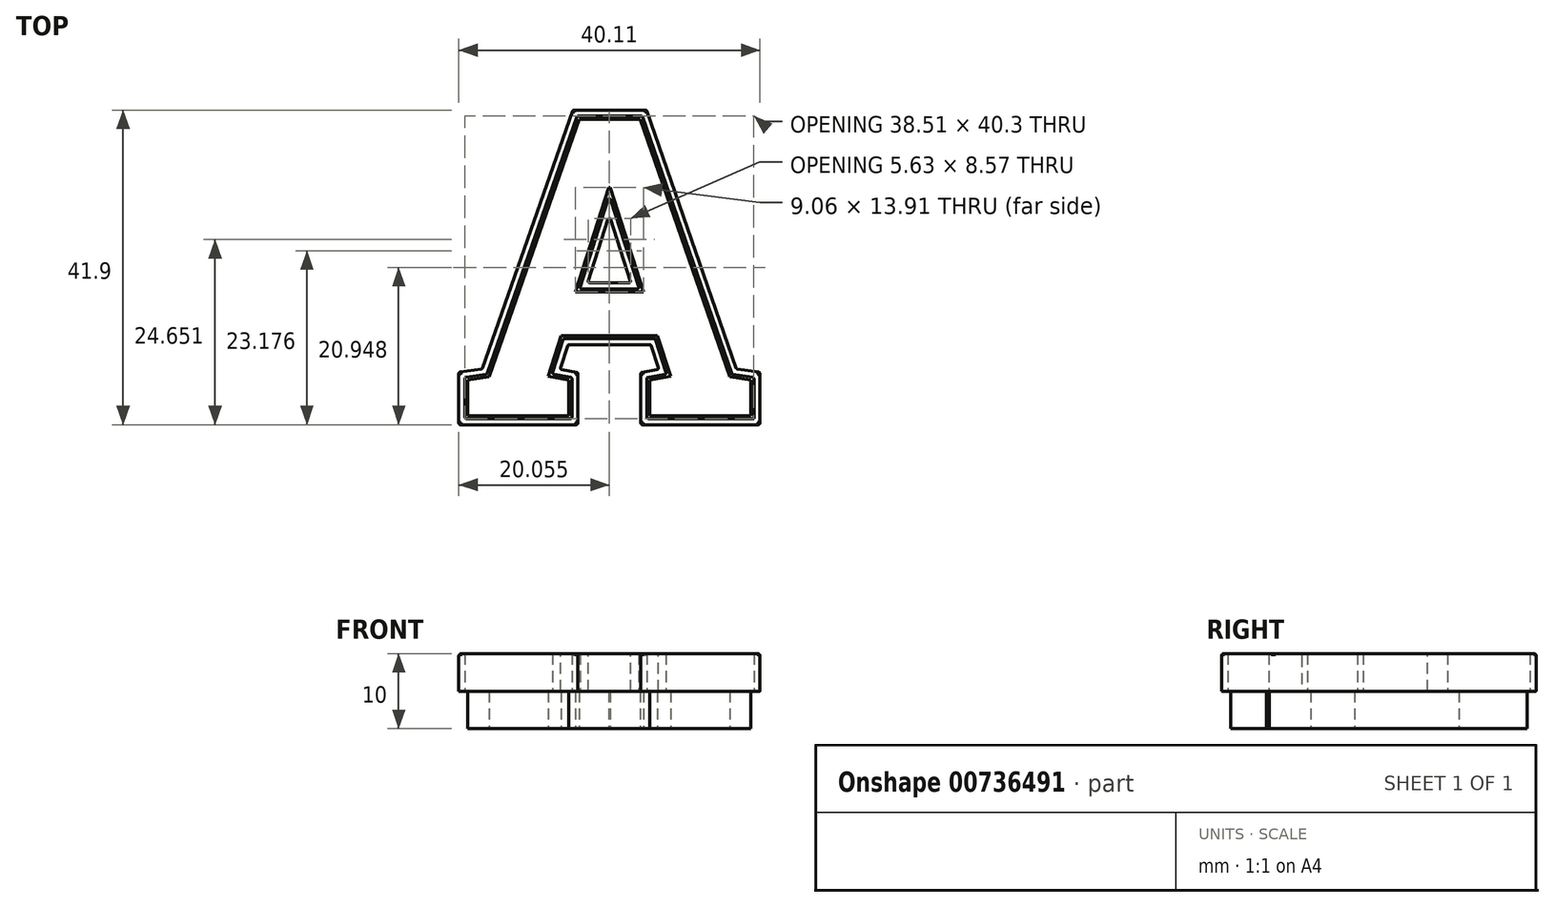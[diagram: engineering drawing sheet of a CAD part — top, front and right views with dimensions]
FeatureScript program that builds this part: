
annotation { "Feature Type Name" : "Feature", "Feature Type Description" : "" }
export const myFeature = defineFeature(function(context is Context, id is Id, definition is map)
    precondition{}
    {
        {
            var Q0;
            Q0=qCreatedBy(makeId("Top.planeOp"),FACE);
            var sketch = newSketch(context, id + "F0", { "sketchPlane" : qUnion([Q0])});
            skText(sketch, "E0", { "text": "A", "fontName": "RobotoSlab-Bold.ttf"});
            const initialGuessF0  = {"E0": [0, -0.04, 1, 0, 0.04]};
            skSetInitialGuess(sketch, initialGuessF0);
            skSolve(sketch);
        }
        {
            var Q0;
            Q0=makeQuery(id+"F0.imprint","IMPRINT",FACE,{"disambiguationData":[TD([[makeQuery(id+"F0.imprint","IMPRINT",EDGE,{"derivedFrom":sQuery(id+"F0.wireOp",EDGE,"25f650ad-e666-423c-a22c-a6101923079f.sketch_text.stroke-0")}),-1.0]])]});
            var Q1;
            Q1=makeQuery(id+"F0.imprint","IMPRINT",FACE,{"disambiguationData":[TD([[makeQuery(id+"F0.imprint","IMPRINT",EDGE,{"derivedFrom":sQuery(id+"F0.wireOp",EDGE,"E0.sketch_text.stroke-0")}),-1.0]])]});
            extrude(context, id + "F1", {"entities" : qUnion([Q0, Q1]), "depth" : 5 * mm, "offsetDistance" : 25 * mm});
        }
        {
            var Q0;
            Q0=makeQuery(id+"F1.opExtrude","CAP_FACE",FACE,{"disambiguationData":[OSD([sQuery(id+"F0.wireOp",EDGE,"E0.sketch_text.stroke-0"),sQuery(id+"F0.wireOp",EDGE,"E0.sketch_text.stroke-1"),sQuery(id+"F0.wireOp",EDGE,"E0.sketch_text.stroke-2"),sQuery(id+"F0.wireOp",EDGE,"E0.sketch_text.stroke-3"),sQuery(id+"F0.wireOp",EDGE,"E0.sketch_text.stroke-4"),sQuery(id+"F0.wireOp",EDGE,"E0.sketch_text.stroke-5"),sQuery(id+"F0.wireOp",EDGE,"E0.sketch_text.stroke-6"),sQuery(id+"F0.wireOp",EDGE,"E0.sketch_text.stroke-7"),sQuery(id+"F0.wireOp",EDGE,"E0.sketch_text.stroke-8"),sQuery(id+"F0.wireOp",EDGE,"E0.sketch_text.stroke-9"),sQuery(id+"F0.wireOp",EDGE,"E0.sketch_text.stroke-10"),sQuery(id+"F0.wireOp",EDGE,"E0.sketch_text.stroke-11"),sQuery(id+"F0.wireOp",EDGE,"E0.sketch_text.stroke-12"),sQuery(id+"F0.wireOp",EDGE,"E0.sketch_text.stroke-13"),sQuery(id+"F0.wireOp",EDGE,"E0.sketch_text.stroke-14"),sQuery(id+"F0.wireOp",EDGE,"E0.sketch_text.stroke-15"),sQuery(id+"F0.wireOp",EDGE,"E0.sketch_text.stroke-16"),sQuery(id+"F0.wireOp",EDGE,"E0.sketch_text.stroke-17"),sQuery(id+"F0.wireOp",EDGE,"E0.sketch_text.stroke-18"),sQuery(id+"F0.wireOp",EDGE,"E0.sketch_text.stroke-19")])],"isStart":false});
            var sketch = newSketch(context, id + "F2", { "sketchPlane" : qUnion([Q0])});
            skLineSegment(sketch, "E1.0", {"start": v(3.63, -34.48) * mm, "end": v(0.71, -34.9) * mm});
            skLineSegment(sketch, "E1.1", {"start": v(15.67, -0.1) * mm, "end": v(3.63, -34.48) * mm});
            skLineSegment(sketch, "E1.2", {"start": v(24.35, -0.1) * mm, "end": v(15.67, -0.1) * mm});
            skLineSegment(sketch, "E1.3", {"start": v(36.3, -34.48) * mm, "end": v(24.35, -0.1) * mm});
            skLineSegment(sketch, "E1.4", {"start": v(39.22, -34.9) * mm, "end": v(36.3, -34.48) * mm});
            skLineSegment(sketch, "E1.5", {"start": v(12.35, -34.45) * mm, "end": v(13.86, -29.74) * mm});
            skLineSegment(sketch, "E1.6", {"start": v(14.97, -34.92) * mm, "end": v(12.35, -34.45) * mm});
            skLineSegment(sketch, "E1.7", {"start": v(14.97, -40.4) * mm, "end": v(14.97, -34.92) * mm});
            skLineSegment(sketch, "E1.8", {"start": v(0.71, -40.4) * mm, "end": v(14.97, -40.4) * mm});
            skLineSegment(sketch, "E1.9", {"start": v(13.86, -29.74) * mm, "end": v(26.08, -29.74) * mm});
            skLineSegment(sketch, "E1.10", {"start": v(26.08, -29.74) * mm, "end": v(27.59, -34.45) * mm});
            skLineSegment(sketch, "E1.11", {"start": v(27.59, -34.45) * mm, "end": v(24.96, -34.92) * mm});
            skLineSegment(sketch, "E1.12", {"start": v(24.96, -34.92) * mm, "end": v(24.96, -40.4) * mm});
            skLineSegment(sketch, "E1.13", {"start": v(24.96, -40.4) * mm, "end": v(39.22, -40.4) * mm});
            skLineSegment(sketch, "E1.14", {"start": v(0.71, -34.9) * mm, "end": v(0.71, -40.4) * mm});
            skLineSegment(sketch, "E1.15", {"start": v(39.22, -40.4) * mm, "end": v(39.22, -34.9) * mm});
            skLineSegment(sketch, "E2.0", {"start": v(19.97, -10.66) * mm, "end": v(15.98, -23.1) * mm});
            skLineSegment(sketch, "E2.1", {"start": v(23.95, -23.1) * mm, "end": v(19.97, -10.66) * mm});
            skLineSegment(sketch, "E2.2", {"start": v(15.98, -23.1) * mm, "end": v(23.95, -23.1) * mm});
            skLineSegment(sketch, "E3.0", {"start": v(3.04, -33.76) * mm, "end": v(-0.09, -34.21) * mm});
            skLineSegment(sketch, "E3.1", {"start": v(15.1, 0.7) * mm, "end": v(3.04, -33.76) * mm});
            skLineSegment(sketch, "E3.2", {"start": v(24.92, 0.7) * mm, "end": v(15.1, 0.7) * mm});
            skLineSegment(sketch, "E3.3", {"start": v(36.9, -33.76) * mm, "end": v(24.92, 0.7) * mm});
            skLineSegment(sketch, "E3.4", {"start": v(40.02, -34.21) * mm, "end": v(36.9, -33.76) * mm});
            skLineSegment(sketch, "E3.5", {"start": v(13.4, -33.82) * mm, "end": v(14.44, -30.54) * mm});
            skLineSegment(sketch, "E3.6", {"start": v(15.77, -34.25) * mm, "end": v(13.4, -33.82) * mm});
            skLineSegment(sketch, "E3.7", {"start": v(15.77, -41.2) * mm, "end": v(15.77, -34.25) * mm});
            skLineSegment(sketch, "E3.8", {"start": v(-0.09, -41.2) * mm, "end": v(15.77, -41.2) * mm});
            skLineSegment(sketch, "E3.9", {"start": v(14.44, -30.54) * mm, "end": v(25.5, -30.54) * mm});
            skLineSegment(sketch, "E3.10", {"start": v(25.5, -30.54) * mm, "end": v(26.55, -33.82) * mm});
            skLineSegment(sketch, "E3.11", {"start": v(26.55, -33.82) * mm, "end": v(24.16, -34.25) * mm});
            skLineSegment(sketch, "E3.12", {"start": v(24.16, -34.25) * mm, "end": v(24.16, -41.2) * mm});
            skLineSegment(sketch, "E3.13", {"start": v(24.16, -41.2) * mm, "end": v(40.02, -41.2) * mm});
            skLineSegment(sketch, "E3.14", {"start": v(-0.09, -34.21) * mm, "end": v(-0.09, -41.2) * mm});
            skLineSegment(sketch, "E3.15", {"start": v(40.02, -41.2) * mm, "end": v(40.02, -34.21) * mm});
            skLineSegment(sketch, "E4.0", {"start": v(19.97, -13.28) * mm, "end": v(17.08, -22.3) * mm});
            skLineSegment(sketch, "E4.1", {"start": v(22.85, -22.3) * mm, "end": v(19.97, -13.28) * mm});
            skLineSegment(sketch, "E4.2", {"start": v(17.08, -22.3) * mm, "end": v(22.85, -22.3) * mm});
            skSolve(sketch);
        }
        {
            var Q0;
            Q0=makeQuery(id+"F2.imprint","IMPRINT",FACE,{"disambiguationData":[TD([[makeQuery(id+"F2.imprint","IMPRINT",EDGE,{"derivedFrom":sQuery(id+"F2.wireOp",EDGE,"E1.0")}),-1.0]])]});
            var Q1;
            Q1=makeQuery(id+"F2.imprint","IMPRINT",FACE,{"disambiguationData":[TD([[makeQuery(id+"F2.imprint","IMPRINT",EDGE,{"derivedFrom":sQuery(id+"F2.wireOp",EDGE,"E2.0")}),1.0]])]});
            extrude(context, id + "F3", {"entities" : qUnion([Q0, Q1]), "depth" : 5 * mm, "offsetDistance" : 25 * mm});
        }
        {
            var Q0;
            Q0=makeQuery(id+"F4.opExtrude","SWEPT_EDGE",EDGE,{"disambiguationData":[OSD([sQuery(id+"FhZuLQ7qmauHvG2_3.wireOp",EDGE,"db5a32d7-670e-4c0c-9fb4-bdd76a87fa27.2"),sQuery(id+"FhZuLQ7qmauHvG2_3.wireOp",EDGE,"db5a32d7-670e-4c0c-9fb4-bdd76a87fa27.3")])]});
            var Q1;
            Q1=makeQuery(id+"F3.opExtrude","SWEPT_EDGE",EDGE,{"disambiguationData":[OSD([sQuery(id+"F2.wireOp",EDGE,"E3.7"),sQuery(id+"F2.wireOp",EDGE,"E3.8")])]});
            var Q2;
            Q2=makeQuery(id+"F3.opExtrude","SWEPT_EDGE",EDGE,{"disambiguationData":[OSD([sQuery(id+"F2.wireOp",EDGE,"E3.8"),sQuery(id+"F2.wireOp",EDGE,"E3.14")])]});
            var Q3;
            Q3=makeQuery(id+"F3.opExtrude","SWEPT_EDGE",EDGE,{"disambiguationData":[OSD([sQuery(id+"F2.wireOp",EDGE,"E3.0"),sQuery(id+"F2.wireOp",EDGE,"E3.14")])]});
            var Q4;
            Q4=makeQuery(id+"F4.opExtrude","SWEPT_EDGE",EDGE,{"disambiguationData":[OSD([sQuery(id+"FhZuLQ7qmauHvG2_3.wireOp",EDGE,"db5a32d7-670e-4c0c-9fb4-bdd76a87fa27.3"),sQuery(id+"FhZuLQ7qmauHvG2_3.wireOp",EDGE,"db5a32d7-670e-4c0c-9fb4-bdd76a87fa27.4")])]});
            var Q5;
            Q5=makeQuery(id+"F4.opExtrude","SWEPT_EDGE",EDGE,{"disambiguationData":[OSD([sQuery(id+"FhZuLQ7qmauHvG2_3.wireOp",EDGE,"db5a32d7-670e-4c0c-9fb4-bdd76a87fa27.4"),sQuery(id+"FhZuLQ7qmauHvG2_3.wireOp",EDGE,"db5a32d7-670e-4c0c-9fb4-bdd76a87fa27.15")])]});
            var Q6;
            Q6=makeQuery(id+"F3.opExtrude","SWEPT_EDGE",EDGE,{"disambiguationData":[OSD([sQuery(id+"F2.wireOp",EDGE,"E3.0"),sQuery(id+"F2.wireOp",EDGE,"E3.1")])]});
            var Q7;
            Q7=makeQuery(id+"F4.opExtrude","SWEPT_EDGE",EDGE,{"disambiguationData":[OSD([sQuery(id+"FhZuLQ7qmauHvG2_3.wireOp",EDGE,"db5a32d7-670e-4c0c-9fb4-bdd76a87fa27.13"),sQuery(id+"FhZuLQ7qmauHvG2_3.wireOp",EDGE,"db5a32d7-670e-4c0c-9fb4-bdd76a87fa27.15")])]});
            var Q8;
            Q8=makeQuery(id+"F4.opExtrude","SWEPT_EDGE",EDGE,{"disambiguationData":[OSD([sQuery(id+"FhZuLQ7qmauHvG2_3.wireOp",EDGE,"db5a32d7-670e-4c0c-9fb4-bdd76a87fa27.12"),sQuery(id+"FhZuLQ7qmauHvG2_3.wireOp",EDGE,"db5a32d7-670e-4c0c-9fb4-bdd76a87fa27.13")])]});
            var Q9;
            Q9=makeQuery(id+"F3.opExtrude","SWEPT_EDGE",EDGE,{"disambiguationData":[OSD([sQuery(id+"F2.wireOp",EDGE,"E3.1"),sQuery(id+"F2.wireOp",EDGE,"E3.2")])]});
            var Q10;
            Q10=makeQuery(id+"F4.opExtrude","SWEPT_EDGE",EDGE,{"disambiguationData":[OSD([sQuery(id+"FhZuLQ7qmauHvG2_3.wireOp",EDGE,"db5a32d7-670e-4c0c-9fb4-bdd76a87fa27.11"),sQuery(id+"FhZuLQ7qmauHvG2_3.wireOp",EDGE,"db5a32d7-670e-4c0c-9fb4-bdd76a87fa27.12")])]});
            var Q11;
            Q11=makeQuery(id+"F3.opExtrude","SWEPT_EDGE",EDGE,{"disambiguationData":[OSD([sQuery(id+"F2.wireOp",EDGE,"E3.2"),sQuery(id+"F2.wireOp",EDGE,"E3.3")])]});
            var Q12;
            Q12=makeQuery(id+"F3.opExtrude","SWEPT_EDGE",EDGE,{"disambiguationData":[OSD([sQuery(id+"F2.wireOp",EDGE,"E2.0"),sQuery(id+"F2.wireOp",EDGE,"E2.1")])]});
            var Q13;
            Q13=makeQuery(id+"F3.opExtrude","SWEPT_EDGE",EDGE,{"disambiguationData":[OSD([sQuery(id+"F2.wireOp",EDGE,"E2.0"),sQuery(id+"F2.wireOp",EDGE,"E2.2")])]});
            var Q14;
            Q14=makeQuery(id+"F3.opExtrude","SWEPT_EDGE",EDGE,{"disambiguationData":[OSD([sQuery(id+"F2.wireOp",EDGE,"E2.1"),sQuery(id+"F2.wireOp",EDGE,"E2.2")])]});
            var Q15;
            Q15=makeQuery(id+"F4.boolean.opBoolean","MERGE",EDGE,{"derivedFrom":[makeQuery(id+"F3.opExtrude","SWEPT_EDGE",EDGE,{"disambiguationData":[OSD([sQuery(id+"F2.wireOp",EDGE,"E4.1"),sQuery(id+"F2.wireOp",EDGE,"E4.2")])]}),makeQuery(id+"F4.opExtrude","SWEPT_EDGE",EDGE,{"disambiguationData":[OSD([sQuery(id+"FhZuLQ7qmauHvG2_3.wireOp",EDGE,"b2817e8e-02ce-4ac3-b8e0-7805fe29df2a.3"),sQuery(id+"FhZuLQ7qmauHvG2_3.wireOp",EDGE,"b2817e8e-02ce-4ac3-b8e0-7805fe29df2a.5")])]})]});
            var Q16;
            Q16=makeQuery(id+"F4.boolean.opBoolean","MERGE",EDGE,{"derivedFrom":[makeQuery(id+"F3.opExtrude","SWEPT_EDGE",EDGE,{"disambiguationData":[OSD([sQuery(id+"F2.wireOp",EDGE,"E4.0"),sQuery(id+"F2.wireOp",EDGE,"E4.1")])]}),makeQuery(id+"F4.opExtrude","SWEPT_EDGE",EDGE,{"disambiguationData":[OSD([sQuery(id+"FhZuLQ7qmauHvG2_3.wireOp",EDGE,"b2817e8e-02ce-4ac3-b8e0-7805fe29df2a.3"),sQuery(id+"FhZuLQ7qmauHvG2_3.wireOp",EDGE,"b2817e8e-02ce-4ac3-b8e0-7805fe29df2a.4"),sQuery(id+"FhZuLQ7qmauHvG2_3.wireOp",EDGE,"JOva3arL-KNf8-qKqD-dtvx-ztHF23ORT1mB"),sQuery(id+"FhZuLQ7qmauHvG2_3.wireOp",EDGE,"FYtEUSBo-1rUa-o7G3-APhZ-UOB6PYPQt5cD")])]})]});
            var Q17;
            Q17=makeQuery(id+"F4.boolean.opBoolean","MERGE",EDGE,{"derivedFrom":[makeQuery(id+"F3.opExtrude","SWEPT_EDGE",EDGE,{"disambiguationData":[OSD([sQuery(id+"F2.wireOp",EDGE,"E4.0"),sQuery(id+"F2.wireOp",EDGE,"E4.2")])]}),makeQuery(id+"F4.opExtrude","SWEPT_EDGE",EDGE,{"disambiguationData":[OSD([sQuery(id+"FhZuLQ7qmauHvG2_3.wireOp",EDGE,"b2817e8e-02ce-4ac3-b8e0-7805fe29df2a.4"),sQuery(id+"FhZuLQ7qmauHvG2_3.wireOp",EDGE,"b2817e8e-02ce-4ac3-b8e0-7805fe29df2a.5")])]})]});
            var Q18;
            Q18=makeQuery(id+"F3.opExtrude","SWEPT_EDGE",EDGE,{"disambiguationData":[OSD([sQuery(id+"F2.wireOp",EDGE,"E3.3"),sQuery(id+"F2.wireOp",EDGE,"E3.4")])]});
            var Q19;
            Q19=makeQuery(id+"F3.opExtrude","SWEPT_EDGE",EDGE,{"disambiguationData":[OSD([sQuery(id+"F2.wireOp",EDGE,"E3.4"),sQuery(id+"F2.wireOp",EDGE,"E3.15")])]});
            var Q20;
            Q20=makeQuery(id+"F4.boolean.opBoolean","MERGE",EDGE,{"derivedFrom":[makeQuery(id+"F3.opExtrude","SWEPT_EDGE",EDGE,{"disambiguationData":[OSD([sQuery(id+"F2.wireOp",EDGE,"E1.12"),sQuery(id+"F2.wireOp",EDGE,"E1.13")])]}),makeQuery(id+"F4.opExtrude","SWEPT_EDGE",EDGE,{"disambiguationData":[OSD([sQuery(id+"FhZuLQ7qmauHvG2_3.wireOp",EDGE,"216b8e4f-3ff4-4a70-9f79-f3512681ab98.5"),sQuery(id+"FhZuLQ7qmauHvG2_3.wireOp",EDGE,"f0158864-78c7-4835-bd51-f915b1f10e7a.1")])]})]});
            var Q21;
            Q21=makeQuery(id+"F4.boolean.opBoolean","MERGE",EDGE,{"derivedFrom":[makeQuery(id+"F3.opExtrude","SWEPT_EDGE",EDGE,{"disambiguationData":[OSD([sQuery(id+"F2.wireOp",EDGE,"E1.10"),sQuery(id+"F2.wireOp",EDGE,"E1.11")])]}),makeQuery(id+"F4.opExtrude","SWEPT_EDGE",EDGE,{"disambiguationData":[OSD([sQuery(id+"FhZuLQ7qmauHvG2_3.wireOp",EDGE,"216b8e4f-3ff4-4a70-9f79-f3512681ab98.0"),sQuery(id+"FhZuLQ7qmauHvG2_3.wireOp",EDGE,"216b8e4f-3ff4-4a70-9f79-f3512681ab98.3")])]})]});
            var Q22;
            Q22=makeQuery(id+"F3.opExtrude","SWEPT_EDGE",EDGE,{"disambiguationData":[OSD([sQuery(id+"F2.wireOp",EDGE,"E1.9"),sQuery(id+"F2.wireOp",EDGE,"E1.10")])]});
            var Q23;
            Q23=makeQuery(id+"F3.opExtrude","SWEPT_EDGE",EDGE,{"disambiguationData":[OSD([sQuery(id+"F2.wireOp",EDGE,"E1.5"),sQuery(id+"F2.wireOp",EDGE,"E1.9")])]});
            var Q24;
            Q24=makeQuery(id+"F4.boolean.opBoolean","MERGE",EDGE,{"derivedFrom":[makeQuery(id+"F3.opExtrude","SWEPT_EDGE",EDGE,{"disambiguationData":[OSD([sQuery(id+"F2.wireOp",EDGE,"E1.5"),sQuery(id+"F2.wireOp",EDGE,"E1.6")])]}),makeQuery(id+"F4.opExtrude","SWEPT_EDGE",EDGE,{"disambiguationData":[OSD([sQuery(id+"FhZuLQ7qmauHvG2_3.wireOp",EDGE,"216b8e4f-3ff4-4a70-9f79-f3512681ab98.1"),sQuery(id+"FhZuLQ7qmauHvG2_3.wireOp",EDGE,"216b8e4f-3ff4-4a70-9f79-f3512681ab98.2")])]})]});
            var Q25;
            Q25=makeQuery(id+"F4.boolean.opBoolean","MERGE",EDGE,{"derivedFrom":[makeQuery(id+"F3.opExtrude","SWEPT_EDGE",EDGE,{"disambiguationData":[OSD([sQuery(id+"F2.wireOp",EDGE,"E1.6"),sQuery(id+"F2.wireOp",EDGE,"E1.7")])]}),makeQuery(id+"F4.opExtrude","SWEPT_EDGE",EDGE,{"disambiguationData":[OSD([sQuery(id+"FhZuLQ7qmauHvG2_3.wireOp",EDGE,"216b8e4f-3ff4-4a70-9f79-f3512681ab98.2"),sQuery(id+"FhZuLQ7qmauHvG2_3.wireOp",EDGE,"216b8e4f-3ff4-4a70-9f79-f3512681ab98.4")])]})]});
            var Q26;
            Q26=makeQuery(id+"F4.boolean.opBoolean","MERGE",EDGE,{"derivedFrom":[makeQuery(id+"F3.opExtrude","SWEPT_EDGE",EDGE,{"disambiguationData":[OSD([sQuery(id+"F2.wireOp",EDGE,"E1.7"),sQuery(id+"F2.wireOp",EDGE,"E1.8")])]}),makeQuery(id+"F4.opExtrude","SWEPT_EDGE",EDGE,{"disambiguationData":[OSD([sQuery(id+"FhZuLQ7qmauHvG2_3.wireOp",EDGE,"216b8e4f-3ff4-4a70-9f79-f3512681ab98.4"),sQuery(id+"FhZuLQ7qmauHvG2_3.wireOp",EDGE,"f0158864-78c7-4835-bd51-f915b1f10e7a.0")])]})]});
            var Q27;
            Q27=makeQuery(id+"F3.opExtrude","SWEPT_EDGE",EDGE,{"disambiguationData":[OSD([sQuery(id+"F2.wireOp",EDGE,"E3.10"),sQuery(id+"F2.wireOp",EDGE,"E3.11")])]});
            var Q28;
            Q28=makeQuery(id+"F3.opExtrude","SWEPT_EDGE",EDGE,{"disambiguationData":[OSD([sQuery(id+"F2.wireOp",EDGE,"E3.11"),sQuery(id+"F2.wireOp",EDGE,"E3.12")])]});
            var Q29;
            Q29=makeQuery(id+"F3.opExtrude","SWEPT_EDGE",EDGE,{"disambiguationData":[OSD([sQuery(id+"F2.wireOp",EDGE,"E3.12"),sQuery(id+"F2.wireOp",EDGE,"E3.13")])]});
            var Q30;
            Q30=makeQuery(id+"F3.opExtrude","SWEPT_EDGE",EDGE,{"disambiguationData":[OSD([sQuery(id+"F2.wireOp",EDGE,"E3.13"),sQuery(id+"F2.wireOp",EDGE,"E3.15")])]});
            var Q31;
            Q31=makeQuery(id+"F4.boolean.opBoolean","MERGE",EDGE,{"derivedFrom":[makeQuery(id+"F3.opExtrude","SWEPT_EDGE",EDGE,{"disambiguationData":[OSD([sQuery(id+"F2.wireOp",EDGE,"E1.4"),sQuery(id+"F2.wireOp",EDGE,"E1.15")])]}),makeQuery(id+"F4.opExtrude","SWEPT_EDGE",EDGE,{"disambiguationData":[OSD([sQuery(id+"FhZuLQ7qmauHvG2_3.wireOp",EDGE,"f0158864-78c7-4835-bd51-f915b1f10e7a.2"),sQuery(id+"FhZuLQ7qmauHvG2_3.wireOp",EDGE,"f0158864-78c7-4835-bd51-f915b1f10e7a.3")])]})]});
            var Q32;
            Q32=makeQuery(id+"F4.boolean.opBoolean","MERGE",EDGE,{"derivedFrom":[makeQuery(id+"F3.opExtrude","SWEPT_EDGE",EDGE,{"disambiguationData":[OSD([sQuery(id+"F2.wireOp",EDGE,"E1.3"),sQuery(id+"F2.wireOp",EDGE,"E1.4")])]}),makeQuery(id+"F4.opExtrude","SWEPT_EDGE",EDGE,{"disambiguationData":[OSD([sQuery(id+"FhZuLQ7qmauHvG2_3.wireOp",EDGE,"f0158864-78c7-4835-bd51-f915b1f10e7a.3"),sQuery(id+"FhZuLQ7qmauHvG2_3.wireOp",EDGE,"f0158864-78c7-4835-bd51-f915b1f10e7a.4")])]})]});
            var Q33;
            Q33=makeQuery(id+"F4.boolean.opBoolean","MERGE",EDGE,{"derivedFrom":[makeQuery(id+"F3.opExtrude","SWEPT_EDGE",EDGE,{"disambiguationData":[OSD([sQuery(id+"F2.wireOp",EDGE,"E1.2"),sQuery(id+"F2.wireOp",EDGE,"E1.3")])]}),makeQuery(id+"F4.opExtrude","SWEPT_EDGE",EDGE,{"disambiguationData":[OSD([sQuery(id+"FhZuLQ7qmauHvG2_3.wireOp",EDGE,"f0158864-78c7-4835-bd51-f915b1f10e7a.4"),sQuery(id+"FhZuLQ7qmauHvG2_3.wireOp",EDGE,"f0158864-78c7-4835-bd51-f915b1f10e7a.8")])]})]});
            var Q34;
            Q34=makeQuery(id+"F4.boolean.opBoolean","MERGE",EDGE,{"derivedFrom":[makeQuery(id+"F3.opExtrude","SWEPT_EDGE",EDGE,{"disambiguationData":[OSD([sQuery(id+"F2.wireOp",EDGE,"E1.1"),sQuery(id+"F2.wireOp",EDGE,"E1.2")])]}),makeQuery(id+"F4.opExtrude","SWEPT_EDGE",EDGE,{"disambiguationData":[OSD([sQuery(id+"FhZuLQ7qmauHvG2_3.wireOp",EDGE,"f0158864-78c7-4835-bd51-f915b1f10e7a.7"),sQuery(id+"FhZuLQ7qmauHvG2_3.wireOp",EDGE,"f0158864-78c7-4835-bd51-f915b1f10e7a.8")])]})]});
            var Q35;
            Q35=makeQuery(id+"F3.opExtrude","SWEPT_EDGE",EDGE,{"disambiguationData":[OSD([sQuery(id+"F2.wireOp",EDGE,"E3.9"),sQuery(id+"F2.wireOp",EDGE,"E3.10")])]});
            var Q36;
            Q36=makeQuery(id+"F3.opExtrude","SWEPT_EDGE",EDGE,{"disambiguationData":[OSD([sQuery(id+"F2.wireOp",EDGE,"E3.5"),sQuery(id+"F2.wireOp",EDGE,"E3.9")])]});
            var Q37;
            Q37=makeQuery(id+"F3.opExtrude","SWEPT_EDGE",EDGE,{"disambiguationData":[OSD([sQuery(id+"F2.wireOp",EDGE,"E3.5"),sQuery(id+"F2.wireOp",EDGE,"E3.6")])]});
            var Q38;
            Q38=makeQuery(id+"F3.opExtrude","SWEPT_EDGE",EDGE,{"disambiguationData":[OSD([sQuery(id+"F2.wireOp",EDGE,"E3.6"),sQuery(id+"F2.wireOp",EDGE,"E3.7")])]});
            var Q39;
            Q39=makeQuery(id+"F4.boolean.opBoolean","MERGE",EDGE,{"derivedFrom":[makeQuery(id+"F3.opExtrude","SWEPT_EDGE",EDGE,{"disambiguationData":[OSD([sQuery(id+"F2.wireOp",EDGE,"E1.0"),sQuery(id+"F2.wireOp",EDGE,"E1.14")])]}),makeQuery(id+"F4.opExtrude","SWEPT_EDGE",EDGE,{"disambiguationData":[OSD([sQuery(id+"FhZuLQ7qmauHvG2_3.wireOp",EDGE,"f0158864-78c7-4835-bd51-f915b1f10e7a.5"),sQuery(id+"FhZuLQ7qmauHvG2_3.wireOp",EDGE,"f0158864-78c7-4835-bd51-f915b1f10e7a.6")])]})]});
            var Q40;
            Q40=makeQuery(id+"F4.boolean.opBoolean","MERGE",EDGE,{"derivedFrom":[makeQuery(id+"F3.opExtrude","SWEPT_EDGE",EDGE,{"disambiguationData":[OSD([sQuery(id+"F2.wireOp",EDGE,"E1.0"),sQuery(id+"F2.wireOp",EDGE,"E1.1")])]}),makeQuery(id+"F4.opExtrude","SWEPT_EDGE",EDGE,{"disambiguationData":[OSD([sQuery(id+"FhZuLQ7qmauHvG2_3.wireOp",EDGE,"f0158864-78c7-4835-bd51-f915b1f10e7a.6"),sQuery(id+"FhZuLQ7qmauHvG2_3.wireOp",EDGE,"f0158864-78c7-4835-bd51-f915b1f10e7a.7")])]})]});
            var Q41;
            Q41=makeQuery(id+"F4.boolean.opBoolean","MERGE",EDGE,{"derivedFrom":[makeQuery(id+"F3.opExtrude","SWEPT_EDGE",EDGE,{"disambiguationData":[OSD([sQuery(id+"F2.wireOp",EDGE,"E1.8"),sQuery(id+"F2.wireOp",EDGE,"E1.14")])]}),makeQuery(id+"F4.opExtrude","SWEPT_EDGE",EDGE,{"disambiguationData":[OSD([sQuery(id+"FhZuLQ7qmauHvG2_3.wireOp",EDGE,"f0158864-78c7-4835-bd51-f915b1f10e7a.0"),sQuery(id+"FhZuLQ7qmauHvG2_3.wireOp",EDGE,"f0158864-78c7-4835-bd51-f915b1f10e7a.5")])]})]});
            var Q42;
            Q42=makeQuery(id+"F4.opExtrude","SWEPT_EDGE",EDGE,{"disambiguationData":[OSD([sQuery(id+"FhZuLQ7qmauHvG2_3.wireOp",EDGE,"db5a32d7-670e-4c0c-9fb4-bdd76a87fa27.5"),sQuery(id+"FhZuLQ7qmauHvG2_3.wireOp",EDGE,"db5a32d7-670e-4c0c-9fb4-bdd76a87fa27.9")])]});
            var Q43;
            Q43=makeQuery(id+"F4.opExtrude","SWEPT_EDGE",EDGE,{"disambiguationData":[OSD([sQuery(id+"FhZuLQ7qmauHvG2_3.wireOp",EDGE,"db5a32d7-670e-4c0c-9fb4-bdd76a87fa27.9"),sQuery(id+"FhZuLQ7qmauHvG2_3.wireOp",EDGE,"db5a32d7-670e-4c0c-9fb4-bdd76a87fa27.10")])]});
            var Q44;
            Q44=makeQuery(id+"F4.opExtrude","SWEPT_EDGE",EDGE,{"disambiguationData":[OSD([sQuery(id+"FhZuLQ7qmauHvG2_3.wireOp",EDGE,"db5a32d7-670e-4c0c-9fb4-bdd76a87fa27.10"),sQuery(id+"FhZuLQ7qmauHvG2_3.wireOp",EDGE,"db5a32d7-670e-4c0c-9fb4-bdd76a87fa27.11")])]});
            var Q45;
            Q45=makeQuery(id+"F4.opExtrude","SWEPT_EDGE",EDGE,{"disambiguationData":[OSD([sQuery(id+"FhZuLQ7qmauHvG2_3.wireOp",EDGE,"db5a32d7-670e-4c0c-9fb4-bdd76a87fa27.5"),sQuery(id+"FhZuLQ7qmauHvG2_3.wireOp",EDGE,"db5a32d7-670e-4c0c-9fb4-bdd76a87fa27.6")])]});
            var Q46;
            Q46=makeQuery(id+"F4.opExtrude","SWEPT_EDGE",EDGE,{"disambiguationData":[OSD([sQuery(id+"FhZuLQ7qmauHvG2_3.wireOp",EDGE,"db5a32d7-670e-4c0c-9fb4-bdd76a87fa27.6"),sQuery(id+"FhZuLQ7qmauHvG2_3.wireOp",EDGE,"db5a32d7-670e-4c0c-9fb4-bdd76a87fa27.7")])]});
            var Q47;
            Q47=makeQuery(id+"F4.opExtrude","SWEPT_EDGE",EDGE,{"disambiguationData":[OSD([sQuery(id+"FhZuLQ7qmauHvG2_3.wireOp",EDGE,"db5a32d7-670e-4c0c-9fb4-bdd76a87fa27.7"),sQuery(id+"FhZuLQ7qmauHvG2_3.wireOp",EDGE,"db5a32d7-670e-4c0c-9fb4-bdd76a87fa27.8")])]});
            var Q48;
            Q48=makeQuery(id+"F4.opExtrude","SWEPT_EDGE",EDGE,{"disambiguationData":[OSD([sQuery(id+"FhZuLQ7qmauHvG2_3.wireOp",EDGE,"db5a32d7-670e-4c0c-9fb4-bdd76a87fa27.8"),sQuery(id+"FhZuLQ7qmauHvG2_3.wireOp",EDGE,"db5a32d7-670e-4c0c-9fb4-bdd76a87fa27.14")])]});
            var Q49;
            Q49=makeQuery(id+"F4.opExtrude","SWEPT_EDGE",EDGE,{"disambiguationData":[OSD([sQuery(id+"FhZuLQ7qmauHvG2_3.wireOp",EDGE,"db5a32d7-670e-4c0c-9fb4-bdd76a87fa27.0"),sQuery(id+"FhZuLQ7qmauHvG2_3.wireOp",EDGE,"db5a32d7-670e-4c0c-9fb4-bdd76a87fa27.14")])]});
            var Q50;
            Q50=makeQuery(id+"F4.opExtrude","SWEPT_EDGE",EDGE,{"disambiguationData":[OSD([sQuery(id+"FhZuLQ7qmauHvG2_3.wireOp",EDGE,"db5a32d7-670e-4c0c-9fb4-bdd76a87fa27.1"),sQuery(id+"FhZuLQ7qmauHvG2_3.wireOp",EDGE,"db5a32d7-670e-4c0c-9fb4-bdd76a87fa27.2")])]});
            var Q51;
            Q51=makeQuery(id+"F4.opExtrude","SWEPT_EDGE",EDGE,{"disambiguationData":[OSD([sQuery(id+"FhZuLQ7qmauHvG2_3.wireOp",EDGE,"db5a32d7-670e-4c0c-9fb4-bdd76a87fa27.0"),sQuery(id+"FhZuLQ7qmauHvG2_3.wireOp",EDGE,"db5a32d7-670e-4c0c-9fb4-bdd76a87fa27.1")])]});
            fillet(context, id + "F5", {"entities" : qUnion([Q0, Q1, Q2, Q3, Q4, Q5, Q6, Q7, Q8, Q9, Q10, Q11, Q12, Q13, Q14, Q15, Q16, Q17, Q18, Q19, Q20, Q21, Q22, Q23, Q24, Q25, Q26, Q27, Q28, Q29, Q30, Q31, Q32, Q33, Q34, Q35, Q36, Q37, Q38, Q39, Q40, Q41, Q42, Q43, Q44, Q45, Q46, Q47, Q48, Q49, Q50, Q51]), "radius" : 0.2 * mm, "tangentPropagation" : true, "allowEdgeOverflow" : false});
        }
        {
            var Q0;
            Q0=makeQuery(id+"F3.opExtrude","CAP_EDGE",EDGE,{"disambiguationData":[OSD([sQuery(id+"F2.wireOp",EDGE,"E3.8")])],"isStart":false});
            fillet(context, id + "F6", {"entities" : qUnion([Q0]), "radius" : 0.3 * mm, "tangentPropagation" : true, "allowEdgeOverflow" : false});
        }
    });
